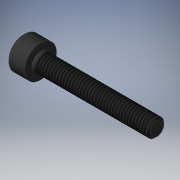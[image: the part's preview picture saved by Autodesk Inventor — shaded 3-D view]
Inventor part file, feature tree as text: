
AUTODESK INVENTOR PART (.ipt)
format: ipt  version: 2019 (Build 230136000, 136)  size: 148,480 bytes
history: native  units: mm
features: other x14, sketch x3, revolve x1, thread x1, hole x1, extrude x1
ambient origin geometry x8: Origin, YZ Plane, XZ Plane, XY Plane, X Axis, Y Axis, Z Axis, Center Point
bodies: Solid1 (feature_tree)
feature tree (21):
  revolve  "Revolution1"  [1 undecoded]
  thread  "Thread1"  [1 undecoded]
  hole  "Hole1"  [1 undecoded]
  extrude  "Extrusion1"  [1 undecoded]
  other  "bolt_XY"
  other  "bolt_YZ"
  other  "bolt_ZX"
  other  "bolt_X"
  other  "bolt_Y"
  other  "bolt_Z"
  other  "bolt_Center"
  other  "nut_XY"
  other  "nut_YZ"
  other  "nut_ZX"
  other  "nut_X"
  other  "nut_Y"
  other  "nut_Z"
  other  "nut_Center"
  sketch  "Sketch_1"  dims[d0=360.0deg d1=19.5mm d2=0.5mm]
  sketch  "Sketch2"  dims[d3=2.5mm d4=6.0mm d5=4.0mm d6=2.0mm d7=90.0deg d8=1.3mm d9=120.0deg d10=1.3mm d11=0.0mm]
  sketch  "Sketch_3"  dims[d12=0.0mm d13=0.0mm]
note: 4 required parameter values undecoded (feature->parameter linkage not recoverable at this tier; creation-order binding heuristic only, values carry confidence <= 0.55)